# Revit family: LB Ottoman
name_source: partatom
category: Furniture
units: mm (PartAtom-declared; Revit-internal decimal feet)

## family parameters
Always vertical = Yes
Cut with Voids When Loaded = No
OmniClass Number = 23.40.20.00
OmniClass Title = General Furniture and Specialties
Room Calculation Point = No
Shared = No
Work Plane-Based = No

## types (6) — shared parameters
Default Elevation = 0' - 0"
Manufacturer = AIS Inc
Product = LB OTTOMAN
URL = https://www.ais-inc.com

## per-type parameters (varying)
| type | Description |
| F-VO182424 | 24Wx24Dx18H LB Ottoman with Feet |
| F-VO182424C | 24Wx24Dx18H LB Ottoman with Casters |
| F-VO183024 | 30Wx24Dx18H LB Ottoman with Feet |
| F-VO183024C | 30Wx24Dx18H LB Ottoman with Casters |
| F-VO183030 | 30Wx30Dx18H LB Ottoman with Feet |
| F-VO183030C | 30Wx30Dx18H LB Ottoman with Casters |

note: column(s) folded — value = type name in every type: Model

type visibility flags: 6 boolean params named "<type name>" — each type sets only its own to Yes (folded from table)

## geometry (parser evidence)
native form markers: Blend x4, Sweep x1
no freeform markers — native parametric forms only
